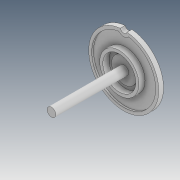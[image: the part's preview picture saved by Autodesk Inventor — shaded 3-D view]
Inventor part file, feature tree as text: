
AUTODESK INVENTOR PART (.ipt)
format: ipt  version: 2020 (Build 240168000, 168)  size: 140,288 bytes
history: native  units: mm
features: extrude x6, sketch x6, plane x3, projected_geometry x1
ambient origin geometry x8: Origin, YZ Plane, XZ Plane, XY Plane, X Axis, Y Axis, Z Axis, Center Point
bodies: Solid1 (feature_tree)
feature tree (16):
  extrude  "Extrusion1"  Depth=1.0mm TaperAngle=0.0deg
  plane  "Work Plane1"
  extrude  "Extrusion3"  Depth=10.75mm
  plane  "Work Plane3"
  extrude  "Extrusion4"  Depth=2.0mm
  plane  "Work Plane2"
  extrude  "Extrusion5"  Depth=24.1mm
  extrude  "Extrusion6"  Depth=0.4mm
  extrude  "Extrusion7"  Depth=1.0mm
  sketch  "Sketch1"  dims[d0=22.8mm d1=1.0mm d2=0.0mm]
  sketch  "Sketch3"  dims[d6=12.75mm d7=10.75mm]
  sketch  "Sketch4"  dims[d8=2.0mm d9=0.0mm d10=2.85mm]
  sketch  "Sketch5"  dims[d11=24.1mm d12=0.0mm d14=8.25mm]
  sketch  "Sketch7"  dims[d15=0.4mm d16=0.0mm d17=2.2mm d18=0.8mm]
  sketch  "Sketch8"  dims[d19=10.0mm d20=0.0mm d21=1.0mm d22=0.57mm d23=0.0mm]
  projected_geometry  "Projected Loop2"
